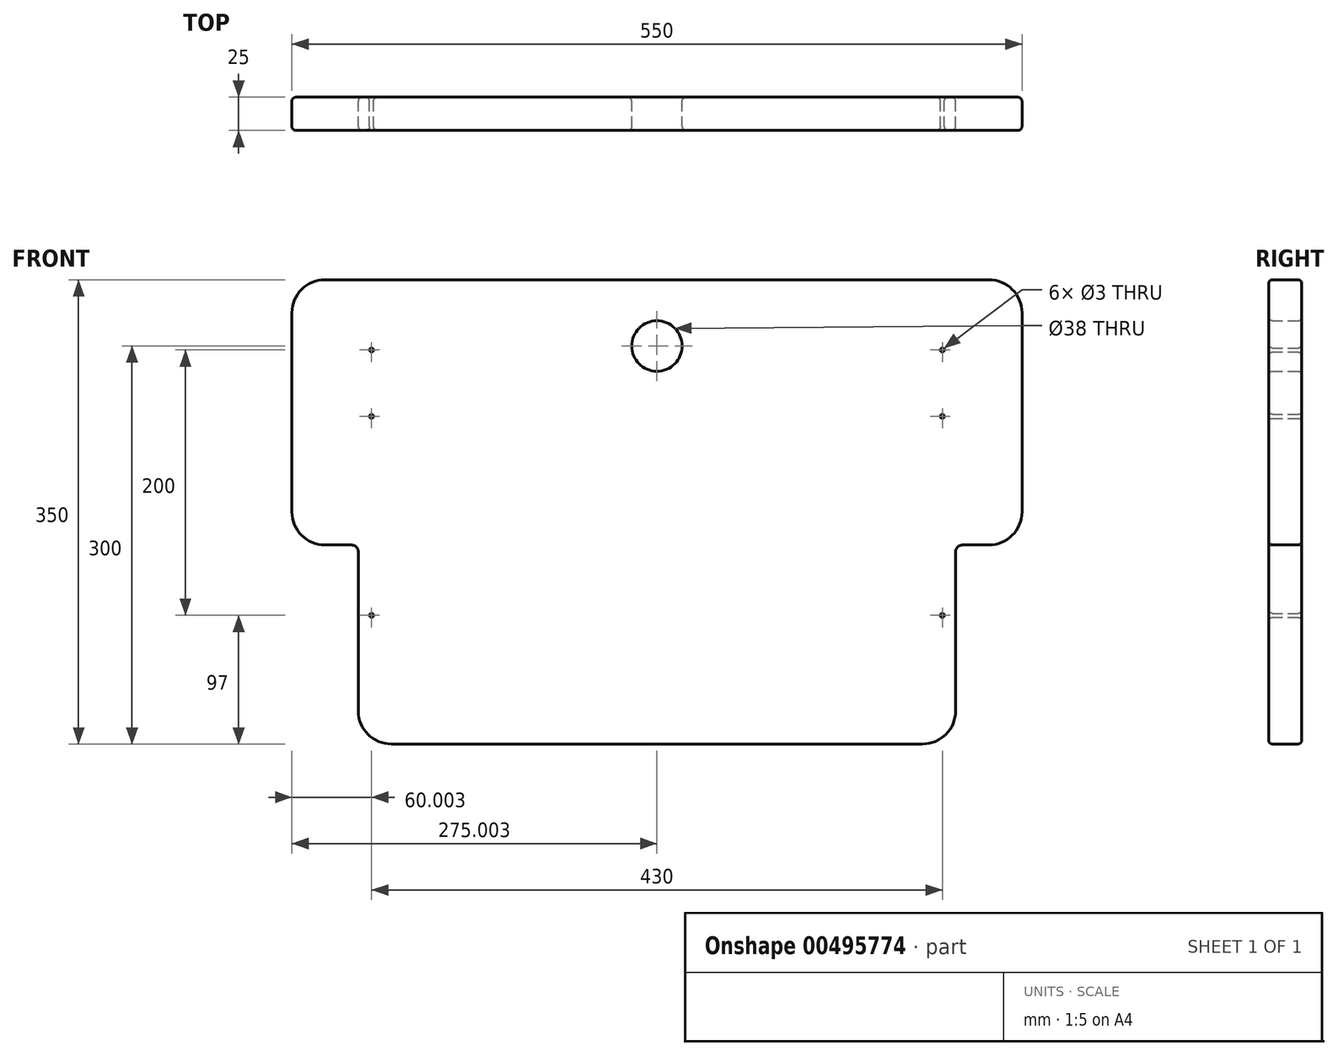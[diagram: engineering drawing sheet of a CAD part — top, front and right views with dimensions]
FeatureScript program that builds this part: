
annotation { "Feature Type Name" : "Feature", "Feature Type Description" : "" }
export const myFeature = defineFeature(function(context is Context, id is Id, definition is map)
    precondition{}
    {
        {
            var Q0;
            Q0=qCreatedBy(makeId("Front.planeOp"),FACE);
            var sketch = newSketch(context, id + "F0", { "sketchPlane" : qUnion([Q0])});
            skLineSegment(sketch, "E0.bottom", {"start": v(-272.42, 253) * mm, "end": v(-22.42, 253) * mm});
            skLineSegment(sketch, "E0.top", {"start": v(-222.42, -97) * mm, "end": v(-22.42, -97) * mm});
            skLineSegment(sketch, "E0.left", {"start": v(-297.42, 228) * mm, "end": v(-297.42, 78) * mm});
            skLineSegment(sketch, "E1", {"start": v(-252.42, 53) * mm, "end": v(-252.42, 53) * mm});
            skLineSegment(sketch, "E2", {"start": v(-247.42, 48) * mm, "end": v(-247.42, -72) * mm});
            skPoint(sketch, "E3.visualSharp", {"position": v(-297.42, 253) * mm});
            skArc(sketch, "E3.filletArc", {"start": v(-272.42, 253) * mm, "mid": v(-290.1, 245.68) * mm, "end": v(-297.42, 228) * mm});
            skPoint(sketch, "E4.visualSharp", {"position": v(-297.42, 53) * mm});
            skPoint(sketch, "E5.visualSharp", {"position": v(-247.42, 53) * mm});
            skPoint(sketch, "E6.visualSharp", {"position": v(-247.42, -97) * mm});
            skArc(sketch, "E6.filletArc", {"start": v(-247.42, -72) * mm, "mid": v(-240.1, -89.68) * mm, "end": v(-222.42, -97) * mm});
            skLineSegment(sketch, "E7", {"start": v(-297.42, 78) * mm, "end": v(-297.42, 78) * mm});
            skLineSegment(sketch, "E8", {"start": v(-247.42, 48) * mm, "end": v(-247.42, 42.72) * mm});
            skLineSegment(sketch, "E9", {"start": v(-272.42, 53) * mm, "end": v(-252.42, 53) * mm});
            skArc(sketch, "E10.filletArc", {"start": v(-297.42, 78) * mm, "mid": v(-290.1, 60.32) * mm, "end": v(-272.42, 53) * mm});
            skArc(sketch, "E11.filletArc", {"start": v(-247.42, 48) * mm, "mid": v(-248.88, 51.54) * mm, "end": v(-252.42, 53) * mm});
            skCircle(sketch, "E12", {"center": v(-237.42, 200) * mm, "radius": 1.5 * mm});
            skCircle(sketch, "E13", {"center": v(-237.42, 150) * mm, "radius": 1.5 * mm});
            skCircle(sketch, "E14", {"center": v(-237.42, 0) * mm, "radius": 1.5 * mm});
            skCircle(sketch, "E15", {"center": v(-22.42, 203) * mm, "radius": 19 * mm});
            skLineSegment(sketch, "E16", {"start": v(-22.42, 253) * mm, "end": v(-22.42, 203) * mm});
            skLineSegment(sketch, "E17.MirrorCS", {"start": v(227.58, 253) * mm, "end": v(-22.42, 253) * mm});
            skPoint(sketch, "E18.MirrorP", {"position": v(252.58, 253) * mm});
            skLineSegment(sketch, "E19.MirrorCS", {"start": v(252.58, 228) * mm, "end": v(252.58, 78) * mm});
            skLineSegment(sketch, "E20.MirrorCS", {"start": v(202.58, 48) * mm, "end": v(202.58, -72) * mm});
            skArc(sketch, "E21.MirrorCS", {"start": v(252.58, 78) * mm, "mid": v(245.26, 60.32) * mm, "end": v(227.58, 53) * mm});
            skArc(sketch, "E22.MirrorCS", {"start": v(227.58, 253) * mm, "mid": v(245.26, 245.68) * mm, "end": v(252.58, 228) * mm});
            skArc(sketch, "E23.MirrorCS", {"start": v(202.58, 48) * mm, "mid": v(204.05, 51.54) * mm, "end": v(207.58, 53) * mm});
            skLineSegment(sketch, "E24.MirrorCS", {"start": v(227.58, 53) * mm, "end": v(207.58, 53) * mm});
            skArc(sketch, "E25.MirrorCS", {"start": v(202.58, -72) * mm, "mid": v(195.26, -89.68) * mm, "end": v(177.58, -97) * mm});
            skLineSegment(sketch, "E26.MirrorCS", {"start": v(177.58, -97) * mm, "end": v(-22.42, -97) * mm});
            skCircle(sketch, "E27.MirrorC", {"center": v(192.58, 0) * mm, "radius": 1.5 * mm});
            skCircle(sketch, "E28.MirrorC", {"center": v(192.58, 150) * mm, "radius": 1.5 * mm});
            skCircle(sketch, "E29.MirrorC", {"center": v(192.58, 200) * mm, "radius": 1.5 * mm});
            skSolve(sketch);
        }
        {
            var Q0;
            Q0 = qSketchRegion(id + "F0", true);
            extrude(context, id + "F1", {"entities" : qUnion([Q0]), "depth" : 25 * mm});
        }
        {
            var Q0;
            Q0=makeQuery(id+"F1.opExtrude","CAP_FACE",FACE,{"disambiguationData":[OSD([sQuery(id+"F0.wireOp",EDGE,"E0.bottom"),sQuery(id+"F0.wireOp",EDGE,"E0.top"),sQuery(id+"F0.wireOp",EDGE,"E0.left"),sQuery(id+"F0.wireOp",EDGE,"E0.right"),sQuery(id+"F0.wireOp",EDGE,"E2"),sQuery(id+"F0.wireOp",EDGE,"0gaUfODG-WZ17-2ITi-n4Cq-07QKSGSHmd1W"),sQuery(id+"F0.wireOp",EDGE,"E3.filletArc"),sQuery(id+"F0.wireOp",EDGE,"38d295fe-4c58-4d10-8b0d-fbdadf300fb1.filletArc"),sQuery(id+"F0.wireOp",EDGE,"E6.filletArc"),sQuery(id+"F0.wireOp",EDGE,"14b4ca6e-53b2-4a05-bd05-d7321e645745.filletArc"),sQuery(id+"F0.wireOp",EDGE,"E8"),sQuery(id+"F0.wireOp",EDGE,"E9"),sQuery(id+"F0.wireOp",EDGE,"XxX32mtm-YITj-vJLa-37Jj-HvCL4x74z33d"),sQuery(id+"F0.wireOp",EDGE,"jlatlvIC-nz9P-8y9b-z9mE-7cLAV2ZDpJaY"),sQuery(id+"F0.wireOp",EDGE,"E10.filletArc"),sQuery(id+"F0.wireOp",EDGE,"2b178d27-9903-49bd-a18a-24e95ab65fbd.filletArc"),sQuery(id+"F0.wireOp",EDGE,"E11.filletArc"),sQuery(id+"F0.wireOp",EDGE,"a8aa6788-3f29-439d-9fad-5e5bea324198.filletArc"),sQuery(id+"F0.wireOp",EDGE,"E12"),sQuery(id+"F0.wireOp",EDGE,"E13"),sQuery(id+"F0.wireOp",EDGE,"E14"),sQuery(id+"F0.wireOp",EDGE,"f5d04c96-5901-4da5-abaf-812db8bbc0540.MirrorC"),sQuery(id+"F0.wireOp",EDGE,"6af07bbd-4161-41cf-9b71-5f36f4a411a80.MirrorC"),sQuery(id+"F0.wireOp",EDGE,"143a584f-dc7e-4f79-b7e9-b5a74a09ddbb0.MirrorC"),sQuery(id+"F0.wireOp",EDGE,"E15")])],"isStart":false});
            var Q1;
            Q1=makeQuery(id+"F1.opExtrude","CAP_FACE",FACE,{"disambiguationData":[OSD([sQuery(id+"F0.wireOp",EDGE,"E0.bottom"),sQuery(id+"F0.wireOp",EDGE,"E0.top"),sQuery(id+"F0.wireOp",EDGE,"E0.left"),sQuery(id+"F0.wireOp",EDGE,"E0.right"),sQuery(id+"F0.wireOp",EDGE,"E2"),sQuery(id+"F0.wireOp",EDGE,"0gaUfODG-WZ17-2ITi-n4Cq-07QKSGSHmd1W"),sQuery(id+"F0.wireOp",EDGE,"E3.filletArc"),sQuery(id+"F0.wireOp",EDGE,"38d295fe-4c58-4d10-8b0d-fbdadf300fb1.filletArc"),sQuery(id+"F0.wireOp",EDGE,"E6.filletArc"),sQuery(id+"F0.wireOp",EDGE,"14b4ca6e-53b2-4a05-bd05-d7321e645745.filletArc"),sQuery(id+"F0.wireOp",EDGE,"E8"),sQuery(id+"F0.wireOp",EDGE,"E9"),sQuery(id+"F0.wireOp",EDGE,"XxX32mtm-YITj-vJLa-37Jj-HvCL4x74z33d"),sQuery(id+"F0.wireOp",EDGE,"jlatlvIC-nz9P-8y9b-z9mE-7cLAV2ZDpJaY"),sQuery(id+"F0.wireOp",EDGE,"E10.filletArc"),sQuery(id+"F0.wireOp",EDGE,"2b178d27-9903-49bd-a18a-24e95ab65fbd.filletArc"),sQuery(id+"F0.wireOp",EDGE,"E11.filletArc"),sQuery(id+"F0.wireOp",EDGE,"a8aa6788-3f29-439d-9fad-5e5bea324198.filletArc"),sQuery(id+"F0.wireOp",EDGE,"E12"),sQuery(id+"F0.wireOp",EDGE,"E13"),sQuery(id+"F0.wireOp",EDGE,"E14"),sQuery(id+"F0.wireOp",EDGE,"f5d04c96-5901-4da5-abaf-812db8bbc0540.MirrorC"),sQuery(id+"F0.wireOp",EDGE,"6af07bbd-4161-41cf-9b71-5f36f4a411a80.MirrorC"),sQuery(id+"F0.wireOp",EDGE,"143a584f-dc7e-4f79-b7e9-b5a74a09ddbb0.MirrorC"),sQuery(id+"F0.wireOp",EDGE,"E15")])],"isStart":true});
            fillet(context, id + "F2", {"entities" : qUnion([Q0, Q1]), "radius" : 3 * mm, "tangentPropagation" : true, "allowEdgeOverflow" : false});
        }
    });
